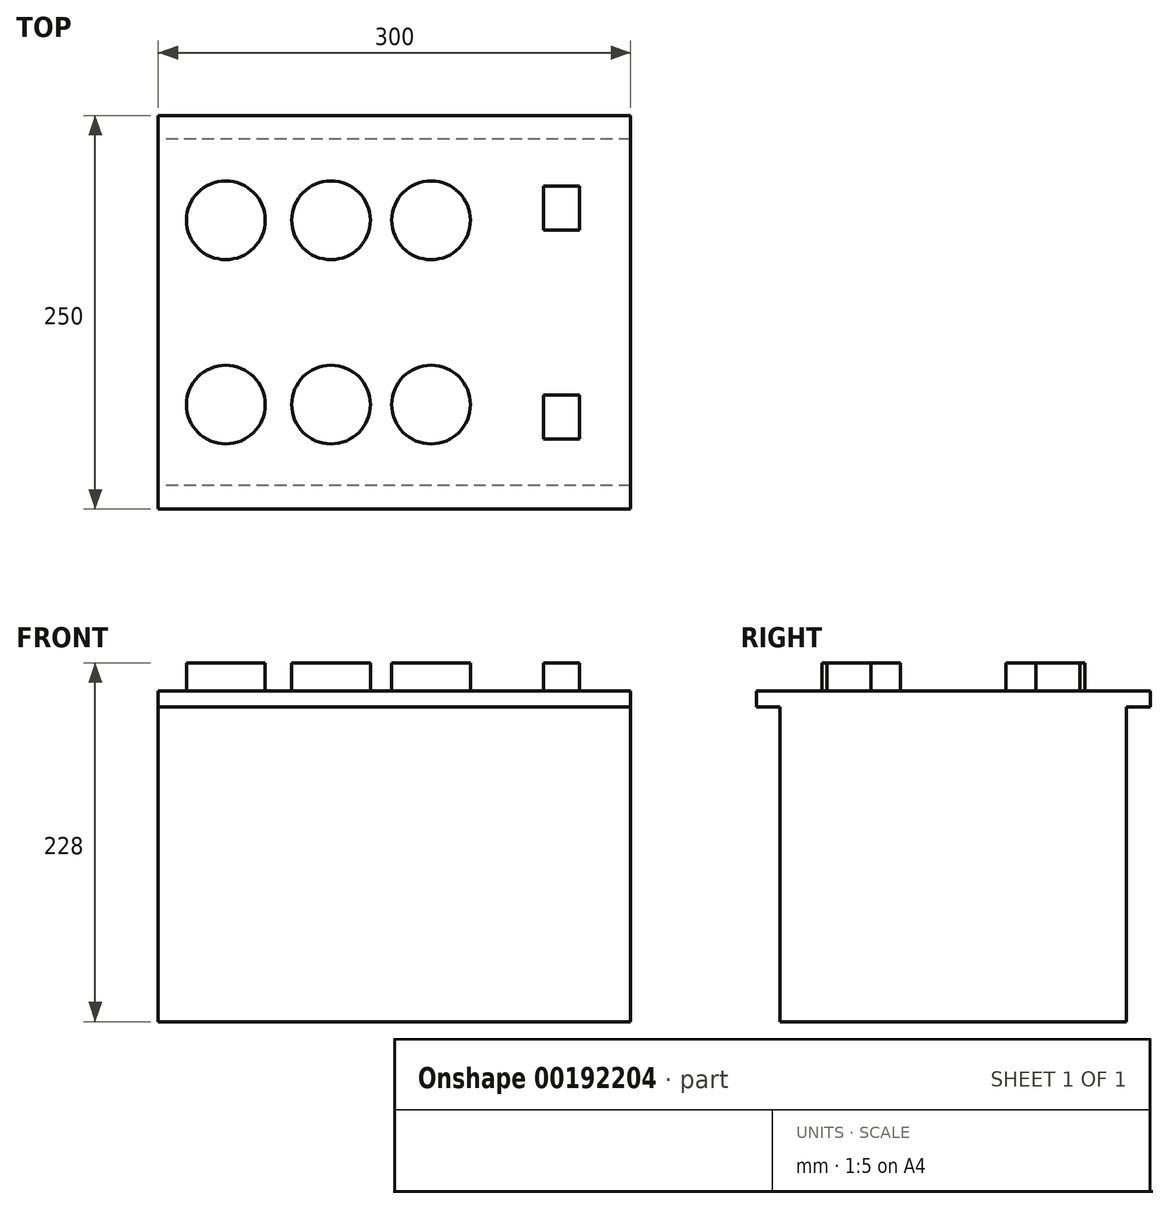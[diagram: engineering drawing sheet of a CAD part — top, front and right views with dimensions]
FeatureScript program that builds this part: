
annotation { "Feature Type Name" : "Feature", "Feature Type Description" : "" }
export const myFeature = defineFeature(function(context is Context, id is Id, definition is map)
    precondition{}
    {
        {
            var Q0;
            Q0=qCreatedBy(makeId("Front.planeOp"),FACE);
            var sketch = newSketch(context, id + "F0", { "sketchPlane" : qUnion([Q0])});
            skLineSegment(sketch, "E0.bottom", {"start": v(150, -100) * mm, "end": v(-150, -100) * mm});
            skLineSegment(sketch, "E0.top", {"start": v(150, 100) * mm, "end": v(-150, 100) * mm});
            skLineSegment(sketch, "E0.left", {"start": v(150, -100) * mm, "end": v(150, 100) * mm});
            skLineSegment(sketch, "E0.right", {"start": v(-150, -100) * mm, "end": v(-150, 100) * mm});
            skPoint(sketch, "E0.middle", {"position": v(0, 0) * mm});
            skSolve(sketch);
        }
        {
            var Q0;
            Q0 = qSketchRegion(id + "F0", true);
            extrude(context, id + "F1", {"entities" : qUnion([Q0]), "depth" : 220 * mm, "symmetric" : true});
        }
        {
            var Q0;
            Q0=makeQuery(id+"F1.opExtrude","SWEPT_FACE",FACE,{"disambiguationData":[OSD([sQuery(id+"F0.wireOp",EDGE,"E0.top")])]});
            var sketch = newSketch(context, id + "F2", { "sketchPlane" : qUnion([Q0])});
            skLineSegment(sketch, "E1.bottom", {"start": v(150, -125) * mm, "end": v(-150, -125) * mm});
            skLineSegment(sketch, "E1.top", {"start": v(150, 125) * mm, "end": v(-150, 125) * mm});
            skLineSegment(sketch, "E1.left", {"start": v(150, -125) * mm, "end": v(150, 125) * mm});
            skLineSegment(sketch, "E1.right", {"start": v(-150, -125) * mm, "end": v(-150, 125) * mm});
            skPoint(sketch, "E1.middle", {"position": v(0, 0) * mm});
            skSolve(sketch);
        }
        {
            var Q0;
            Q0 = qSketchRegion(id + "F2", true);
            extrude(context, id + "F3", {"entities" : qUnion([Q0]), "operationType" : NewBodyOperationType.ADD, "depth" : 10 * mm});
        }
        {
            var Q0;
            Q0=makeQuery(id+"F3.opExtrude","CAP_FACE",FACE,{"disambiguationData":[OSD([sQuery(id+"F2.wireOp",EDGE,"E1.bottom"),sQuery(id+"F2.wireOp",EDGE,"E1.top"),sQuery(id+"F2.wireOp",EDGE,"E1.left"),sQuery(id+"F2.wireOp",EDGE,"E1.right")])],"isStart":false});
            var sketch = newSketch(context, id + "F4", { "sketchPlane" : qUnion([Q0])});
            skCircle(sketch, "E2", {"center": v(-107.1, 58.55) * mm, "radius": 25 * mm});
            skCircle(sketch, "E3", {"center": v(-40.26, 58.55) * mm, "radius": 25 * mm});
            skCircle(sketch, "E4", {"center": v(23.3, 58.55) * mm, "radius": 25 * mm});
            skLineSegment(sketch, "E5", {"start": v(-150, 0) * mm, "end": v(150, 0) * mm});
            skCircle(sketch, "E6.MirrorC", {"center": v(-107.1, -58.55) * mm, "radius": 25 * mm});
            skCircle(sketch, "E7.MirrorC", {"center": v(-40.26, -58.55) * mm, "radius": 25 * mm});
            skCircle(sketch, "E8.MirrorC", {"center": v(23.3, -58.55) * mm, "radius": 25 * mm});
            skLineSegment(sketch, "E9.bottom", {"start": v(117.64, 52.39) * mm, "end": v(94.64, 52.39) * mm});
            skLineSegment(sketch, "E9.top", {"start": v(117.64, 80.39) * mm, "end": v(94.64, 80.39) * mm});
            skLineSegment(sketch, "E9.left", {"start": v(117.64, 52.39) * mm, "end": v(117.64, 80.39) * mm});
            skLineSegment(sketch, "E9.right", {"start": v(94.64, 52.39) * mm, "end": v(94.64, 80.39) * mm});
            skPoint(sketch, "E9.middle", {"position": v(106.14, 66.39) * mm});
            skLineSegment(sketch, "E10.MirrorCS", {"start": v(117.64, -52.39) * mm, "end": v(94.64, -52.39) * mm});
            skLineSegment(sketch, "E11.MirrorCS", {"start": v(117.64, -52.39) * mm, "end": v(117.64, -80.39) * mm});
            skLineSegment(sketch, "E12.MirrorCS", {"start": v(94.64, -52.39) * mm, "end": v(94.64, -80.39) * mm});
            skLineSegment(sketch, "E13.MirrorCS", {"start": v(117.64, -80.39) * mm, "end": v(94.64, -80.39) * mm});
            skSolve(sketch);
        }
        {
            var Q0;
            Q0 = qSketchRegion(id + "F4", true);
            extrude(context, id + "F5", {"entities" : qUnion([Q0]), "operationType" : NewBodyOperationType.ADD, "depth" : 18 * mm});
        }
    });
